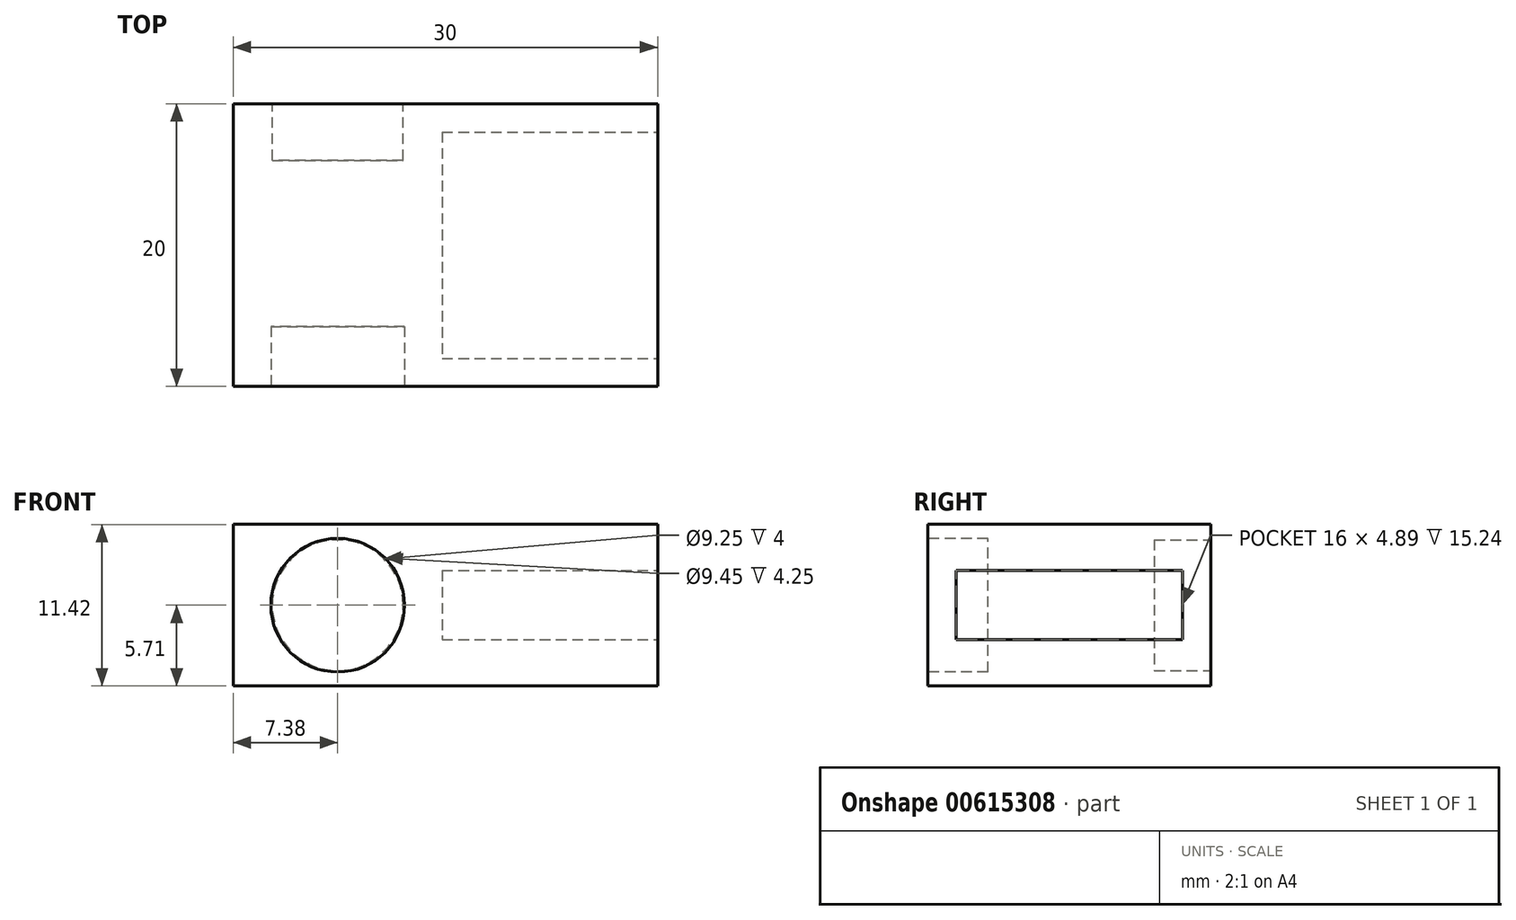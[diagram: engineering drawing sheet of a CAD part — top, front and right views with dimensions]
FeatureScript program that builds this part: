
annotation { "Feature Type Name" : "Feature", "Feature Type Description" : "" }
export const myFeature = defineFeature(function(context is Context, id is Id, definition is map)
    precondition{}
    {
        {
            var Q0;
            Q0=qCreatedBy(makeId("Top.planeOp"),FACE);
            var sketch = newSketch(context, id + "F0", { "sketchPlane" : qUnion([Q0])});
            skLineSegment(sketch, "E0.bottom", {"start": v(15, 10) * mm, "end": v(-15, 10) * mm});
            skLineSegment(sketch, "E0.top", {"start": v(15, -10) * mm, "end": v(-15, -10) * mm});
            skLineSegment(sketch, "E0.left", {"start": v(15, 10) * mm, "end": v(15, -10) * mm});
            skLineSegment(sketch, "E0.right", {"start": v(-15, 10) * mm, "end": v(-15, -10) * mm});
            skPoint(sketch, "E0.middle", {"position": v(0, 0) * mm});
            skSolve(sketch);
        }
        {
            var Q0;
            Q0 = qSketchRegion(id + "F0", true);
            extrude(context, id + "F1", {"entities" : qUnion([Q0]), "endBound" : BoundingType.SYMMETRIC, "depth" : 11.43 * mm, "offsetDistance" : 25.4 * mm});
        }
        {
            var Q0;
            Q0=makeQuery(id+"F1.opExtrude","SWEPT_FACE",FACE,{"disambiguationData":[OSD([sQuery(id+"F0.wireOp",EDGE,"E0.left")])]});
            var sketch = newSketch(context, id + "F2", { "sketchPlane" : qUnion([Q0])});
            skLineSegment(sketch, "E1.bottom", {"start": v(8, 2.45) * mm, "end": v(-8, 2.45) * mm});
            skLineSegment(sketch, "E1.top", {"start": v(8, -2.45) * mm, "end": v(-8, -2.45) * mm});
            skLineSegment(sketch, "E1.left", {"start": v(8, 2.45) * mm, "end": v(8, -2.45) * mm});
            skLineSegment(sketch, "E1.right", {"start": v(-8, 2.45) * mm, "end": v(-8, -2.45) * mm});
            skPoint(sketch, "E1.middle", {"position": v(0, 0) * mm});
            skSolve(sketch);
        }
        {
            var Q0;
            Q0 = qSketchRegion(id + "F2", true);
            extrude(context, id + "F3", {"entities" : qUnion([Q0]), "operationType" : NewBodyOperationType.REMOVE, "oppositeDirection" : true, "depth" : 15.24 * mm, "offsetDistance" : 25.4 * mm});
        }
        {
            var Q0;
            Q0=makeQuery(id+"F1.opExtrude","SWEPT_FACE",FACE,{"disambiguationData":[OSD([sQuery(id+"F0.wireOp",EDGE,"E0.bottom")])]});
            var sketch = newSketch(context, id + "F4", { "sketchPlane" : qUnion([Q0])});
            skLineSegment(sketch, "E2.0.0", {"start": v(-15, -2.45) * mm, "end": v(-15, 2.45) * mm});
            skLineSegment(sketch, "E2.0.1", {"start": v(-15, 2.45) * mm, "end": v(0.24, 2.45) * mm});
            skLineSegment(sketch, "E2.0.2", {"start": v(0.24, 2.45) * mm, "end": v(0.24, -2.45) * mm});
            skLineSegment(sketch, "E2.0.3", {"start": v(0.24, -2.45) * mm, "end": v(-15, -2.45) * mm});
            skCircle(sketch, "E3", {"center": v(7.62, 0) * mm, "radius": 4.62 * mm});
            skSolve(sketch);
        }
        {
            var Q0;
            Q0=makeQuery(id+"F4.imprint","IMPRINT",FACE,{"disambiguationData":[TD([[makeQuery(id+"F4.imprint","IMPRINT",EDGE,{"derivedFrom":sQuery(id+"F4.wireOp",EDGE,"E3")}),1.0]])]});
            extrude(context, id + "F5", {"entities" : qUnion([Q0]), "operationType" : NewBodyOperationType.REMOVE, "oppositeDirection" : true, "depth" : 4 * mm, "offsetDistance" : 25.4 * mm});
        }
        {
            var Q0;
            Q0=makeQuery(id+"F1.opExtrude","SWEPT_FACE",FACE,{"disambiguationData":[OSD([sQuery(id+"F0.wireOp",EDGE,"E0.top")])]});
            var sketch = newSketch(context, id + "F6", { "sketchPlane" : qUnion([Q0])});
            skCircle(sketch, "E4.0", {"center": v(-7.62, 0) * mm, "radius": 4.62 * mm});
            skCircle(sketch, "E5", {"center": v(-7.62, 0) * mm, "radius": 4.72 * mm});
            skSolve(sketch);
        }
        {
            var Q0;
            Q0 = qSketchRegion(id + "F6", true);
            var Q1;
            Q1=makeQuery(id+"F6.imprint","IMPRINT",FACE,{"disambiguationData":[TD([[makeQuery(id+"F6.imprint","IMPRINT",EDGE,{"derivedFrom":sQuery(id+"F6.wireOp",EDGE,"E4.0")}),1.0]])]});
            extrude(context, id + "F7", {"entities" : qUnion([Q0, Q1]), "operationType" : NewBodyOperationType.REMOVE, "oppositeDirection" : true, "depth" : 4.25 * mm, "offsetDistance" : 25.4 * mm});
        }
    });
